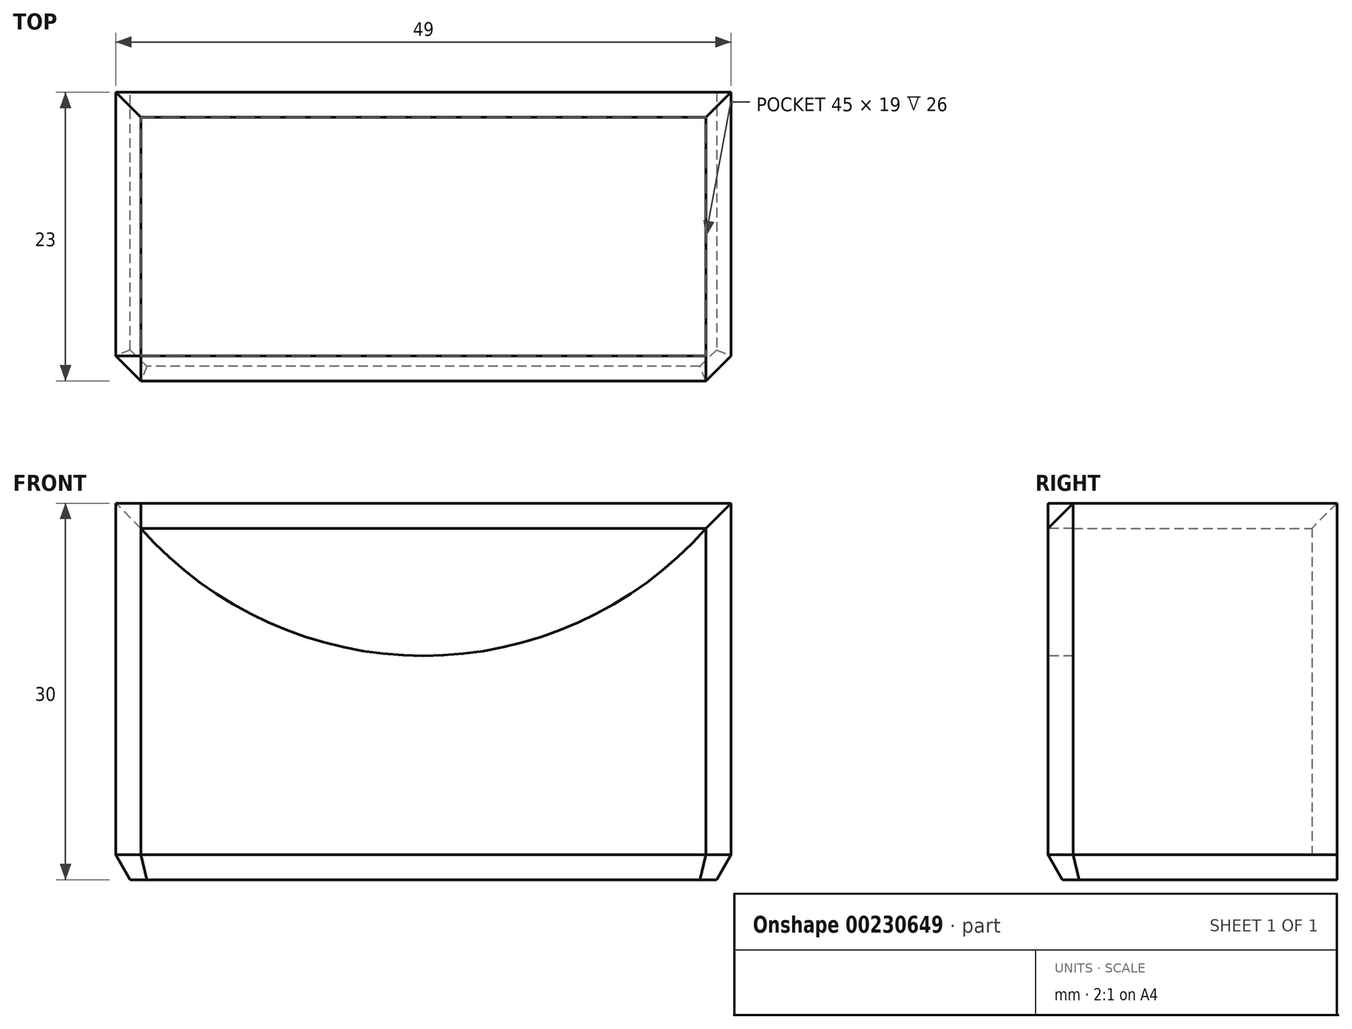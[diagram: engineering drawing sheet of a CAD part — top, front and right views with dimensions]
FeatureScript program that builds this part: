
annotation { "Feature Type Name" : "Feature", "Feature Type Description" : "" }
export const myFeature = defineFeature(function(context is Context, id is Id, definition is map)
    precondition{}
    {
        {
            var Q0;
            Q0=qCreatedBy(makeId("Top.planeOp"),FACE);
            var sketch = newSketch(context, id + "F0", { "sketchPlane" : qUnion([Q0])});
            skLineSegment(sketch, "E0.bottom", {"start": v(24.5, -11.5) * mm, "end": v(-24.5, -11.5) * mm});
            skLineSegment(sketch, "E0.top", {"start": v(24.5, 11.5) * mm, "end": v(-24.5, 11.5) * mm});
            skLineSegment(sketch, "E0.left", {"start": v(24.5, -11.5) * mm, "end": v(24.5, 11.5) * mm});
            skLineSegment(sketch, "E0.right", {"start": v(-24.5, -11.5) * mm, "end": v(-24.5, 11.5) * mm});
            skPoint(sketch, "E0.middle", {"position": v(0, 0) * mm});
            skSolve(sketch);
        }
        {
            var Q0;
            Q0=makeQuery(id+"F0.imprint","IMPRINT",FACE,{"disambiguationData":[TD([[makeQuery(id+"F0.imprint","IMPRINT",EDGE,{"derivedFrom":sQuery(id+"F0.wireOp",EDGE,"E0.bottom")}),-1.0]])]});
            extrude(context, id + "F1", {"entities" : qUnion([Q0]), "depth" : 30 * mm});
        }
        {
            var Q0;
            Q0=makeQuery(id+"F1.opExtrude","CAP_FACE",FACE,{"disambiguationData":[OSD([sQuery(id+"F0.wireOp",EDGE,"E0.bottom"),sQuery(id+"F0.wireOp",EDGE,"E0.top"),sQuery(id+"F0.wireOp",EDGE,"E0.left"),sQuery(id+"F0.wireOp",EDGE,"E0.right")])],"isStart":false});
            shell(context, id + "F2", {"entities" : qUnion([Q0]), "thickness" : 2 * mm});
        }
        {
            var Q0;
            {var subQ0=sQuery(id+"F0.wireOp",EDGE,"E0.top");Q0=makeQuery(id+"F2.opShell","OFFSET_EDGE",EDGE,{"disambiguationData":[OSD([subQ0]),TDD([makeQuery(id+"F1.opExtrude","CAP_EDGE",EDGE,{"disambiguationData":[OSD([subQ0])],"isStart":false})])]});}
            var Q1;
            {var subQ0=sQuery(id+"F0.wireOp",EDGE,"E0.right");Q1=makeQuery(id+"F2.opShell","OFFSET_EDGE",EDGE,{"disambiguationData":[OSD([subQ0]),TDD([makeQuery(id+"F1.opExtrude","CAP_EDGE",EDGE,{"disambiguationData":[OSD([subQ0])],"isStart":false})])]});}
            var Q2;
            {var subQ0=sQuery(id+"F0.wireOp",EDGE,"E0.left");Q2=makeQuery(id+"F2.opShell","OFFSET_EDGE",EDGE,{"disambiguationData":[OSD([subQ0]),TDD([makeQuery(id+"F1.opExtrude","CAP_EDGE",EDGE,{"disambiguationData":[OSD([subQ0])],"isStart":false})])]});}
            chamfer(context, id + "F3", {"entities" : qUnion([Q0, Q1, Q2]), "width" : 2 * mm, "tangentPropagation" : true});
        }
        {
            var Q0;
            Q0=makeQuery(id+"F1.opExtrude","SWEPT_FACE",FACE,{"disambiguationData":[OSD([sQuery(id+"F0.wireOp",EDGE,"E0.bottom")])]});
            var sketch = newSketch(context, id + "F4", { "sketchPlane" : qUnion([Q0])});
            skPoint(sketch, "E1", {"position": v(-22.5, 28) * mm});
            skPoint(sketch, "E2", {"position": v(22.5, 28) * mm});
            skArc(sketch, "E3", {"start": v(-22.5, 28) * mm, "mid": v(0, 17.84) * mm, "end": v(22.5, 28) * mm});
            skLineSegment(sketch, "E4", {"start": v(-22.5, 28) * mm, "end": v(-22.5, 30) * mm});
            skLineSegment(sketch, "E5", {"start": v(22.5, 28) * mm, "end": v(22.5, 30) * mm});
            skSolve(sketch);
        }
        {
            var Q0;
            {var subQ0=sQuery(id+"F4.wireOp",EDGE,"E3");Q0=makeQuery(id+"F4.imprint","IMPRINT",FACE,{"disambiguationData":[TD([[makeQuery(id+"F4.imprint","IMPRINT",EDGE,{"derivedFrom":subQ0}),1.0]])]});}
            extrude(context, id + "F5", {"entities" : qUnion([Q0]), "operationType" : NewBodyOperationType.REMOVE, "endBound" : BoundingType.UP_TO_NEXT, "oppositeDirection" : true, "depth" : 25 * mm});
        }
        {
            var Q0;
            Q0=makeQuery(id+"F5.boolean.opBoolean","COPY",EDGE,{"derivedFrom":makeQuery(id+"F5.opExtrude","SWEPT_EDGE",EDGE,{"disambiguationData":[OSD([sQuery(id+"F0.wireOp",EDGE,"E0.bottom"),sQuery(id+"F4.wireOp",EDGE,"E4")])]})});
            var Q1;
            Q1=makeQuery(id+"F5.boolean.opBoolean","COPY",EDGE,{"derivedFrom":makeQuery(id+"F5.opExtrude","SWEPT_EDGE",EDGE,{"disambiguationData":[OSD([sQuery(id+"F0.wireOp",EDGE,"E0.bottom"),sQuery(id+"F4.wireOp",EDGE,"E5")])]})});
            chamfer(context, id + "F6", {"entities" : qUnion([Q0, Q1]), "width" : 2 * mm, "tangentPropagation" : true});
        }
        {
            var Q0;
            Q0=makeQuery(id+"F1.opExtrude","SWEPT_EDGE",EDGE,{"disambiguationData":[OSD([sQuery(id+"F0.wireOp",EDGE,"E0.bottom"),sQuery(id+"F0.wireOp",EDGE,"E0.right")])]});
            var Q1;
            Q1=makeQuery(id+"F1.opExtrude","SWEPT_EDGE",EDGE,{"disambiguationData":[OSD([sQuery(id+"F0.wireOp",EDGE,"E0.bottom"),sQuery(id+"F0.wireOp",EDGE,"E0.left")])]});
            chamfer(context, id + "F7", {"entities" : qUnion([Q0, Q1]), "width" : 2 * mm, "tangentPropagation" : true});
        }
        {
            var Q0;
            Q0=makeQuery(id+"F1.opExtrude","CAP_EDGE",EDGE,{"disambiguationData":[OSD([sQuery(id+"F0.wireOp",EDGE,"E0.left")])],"isStart":true});
            var Q1;
            {var subQ0=sQuery(id+"F0.wireOp",EDGE,"E0.left");var subQ1=sQuery(id+"F0.wireOp",EDGE,"E0.bottom");Q1=makeQuery(id+"F7.opChamfer","BLEND_EDGE",EDGE,{"blendedFrom":[makeQuery(id+"F1.opExtrude","SWEPT_EDGE",EDGE,{"disambiguationData":[OSD([subQ1,subQ0])]}),makeQuery(id+"F1.opExtrude","CAP_FACE",FACE,{"disambiguationData":[OSD([subQ1,sQuery(id+"F0.wireOp",EDGE,"E0.top"),subQ0,sQuery(id+"F0.wireOp",EDGE,"E0.right")])],"isStart":true})],"blendedInto":[makeQuery(id+"F1.opExtrude","CAP_FACE",FACE,{"disambiguationData":[OSD([subQ1,sQuery(id+"F0.wireOp",EDGE,"E0.top"),subQ0,sQuery(id+"F0.wireOp",EDGE,"E0.right")])],"isStart":true})]});}
            var Q2;
            Q2=makeQuery(id+"F1.opExtrude","CAP_EDGE",EDGE,{"disambiguationData":[OSD([sQuery(id+"F0.wireOp",EDGE,"E0.bottom")])],"isStart":true});
            var Q3;
            {var subQ0=sQuery(id+"F0.wireOp",EDGE,"E0.right");var subQ1=sQuery(id+"F0.wireOp",EDGE,"E0.bottom");Q3=makeQuery(id+"F7.opChamfer","BLEND_EDGE",EDGE,{"blendedFrom":[makeQuery(id+"F1.opExtrude","SWEPT_EDGE",EDGE,{"disambiguationData":[OSD([subQ1,subQ0])]}),makeQuery(id+"F1.opExtrude","CAP_FACE",FACE,{"disambiguationData":[OSD([subQ1,sQuery(id+"F0.wireOp",EDGE,"E0.top"),sQuery(id+"F0.wireOp",EDGE,"E0.left"),subQ0])],"isStart":true})],"blendedInto":[makeQuery(id+"F1.opExtrude","CAP_FACE",FACE,{"disambiguationData":[OSD([subQ1,sQuery(id+"F0.wireOp",EDGE,"E0.top"),sQuery(id+"F0.wireOp",EDGE,"E0.left"),subQ0])],"isStart":true})]});}
            var Q4;
            Q4=makeQuery(id+"F1.opExtrude","CAP_EDGE",EDGE,{"disambiguationData":[OSD([sQuery(id+"F0.wireOp",EDGE,"E0.right")])],"isStart":true});
            chamfer(context, id + "F8", {"entities" : qUnion([Q0, Q1, Q2, Q3, Q4]), "chamferType" : ChamferType.OFFSET_ANGLE, "width" : 2 * mm, "oppositeDirection" : false, "angle" : 30 * degree, "tangentPropagation" : true});
        }
    });
